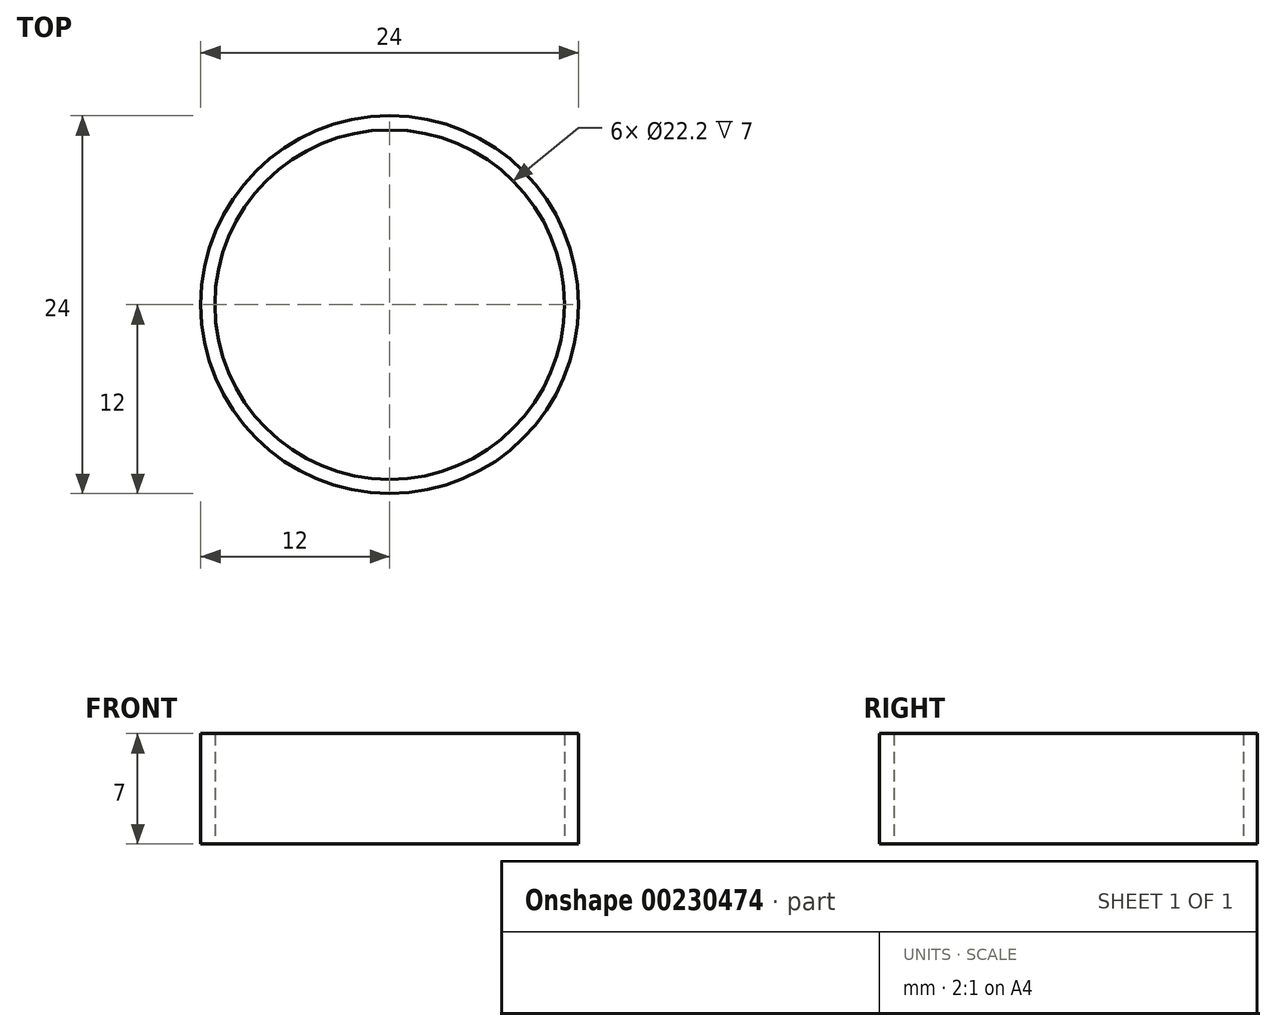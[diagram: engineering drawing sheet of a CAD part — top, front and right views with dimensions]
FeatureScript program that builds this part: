
annotation { "Feature Type Name" : "Feature", "Feature Type Description" : "" }
export const myFeature = defineFeature(function(context is Context, id is Id, definition is map)
    precondition{}
    {
        {
            var Q0;
            Q0=qCreatedBy(makeId("Top.planeOp"),FACE);
            var sketch = newSketch(context, id + "F0", { "sketchPlane" : qUnion([Q0])});
            skCircle(sketch, "E0", {"center": v(0, 0) * mm, "radius": 12 * mm});
            skCircle(sketch, "E1", {"center": v(0, 0) * mm, "radius": 11.1 * mm});
            skSolve(sketch);
        }
        {
            var Q0;
            Q0=makeQuery(id+"F0.imprint","IMPRINT",FACE,{"disambiguationData":[TD([[makeQuery(id+"F0.imprint","IMPRINT",EDGE,{"derivedFrom":sQuery(id+"F0.wireOp",EDGE,"E0")}),1.0]])]});
            extrude(context, id + "F1", {"entities" : qUnion([Q0]), "depth" : 7 * mm});
        }
    });
